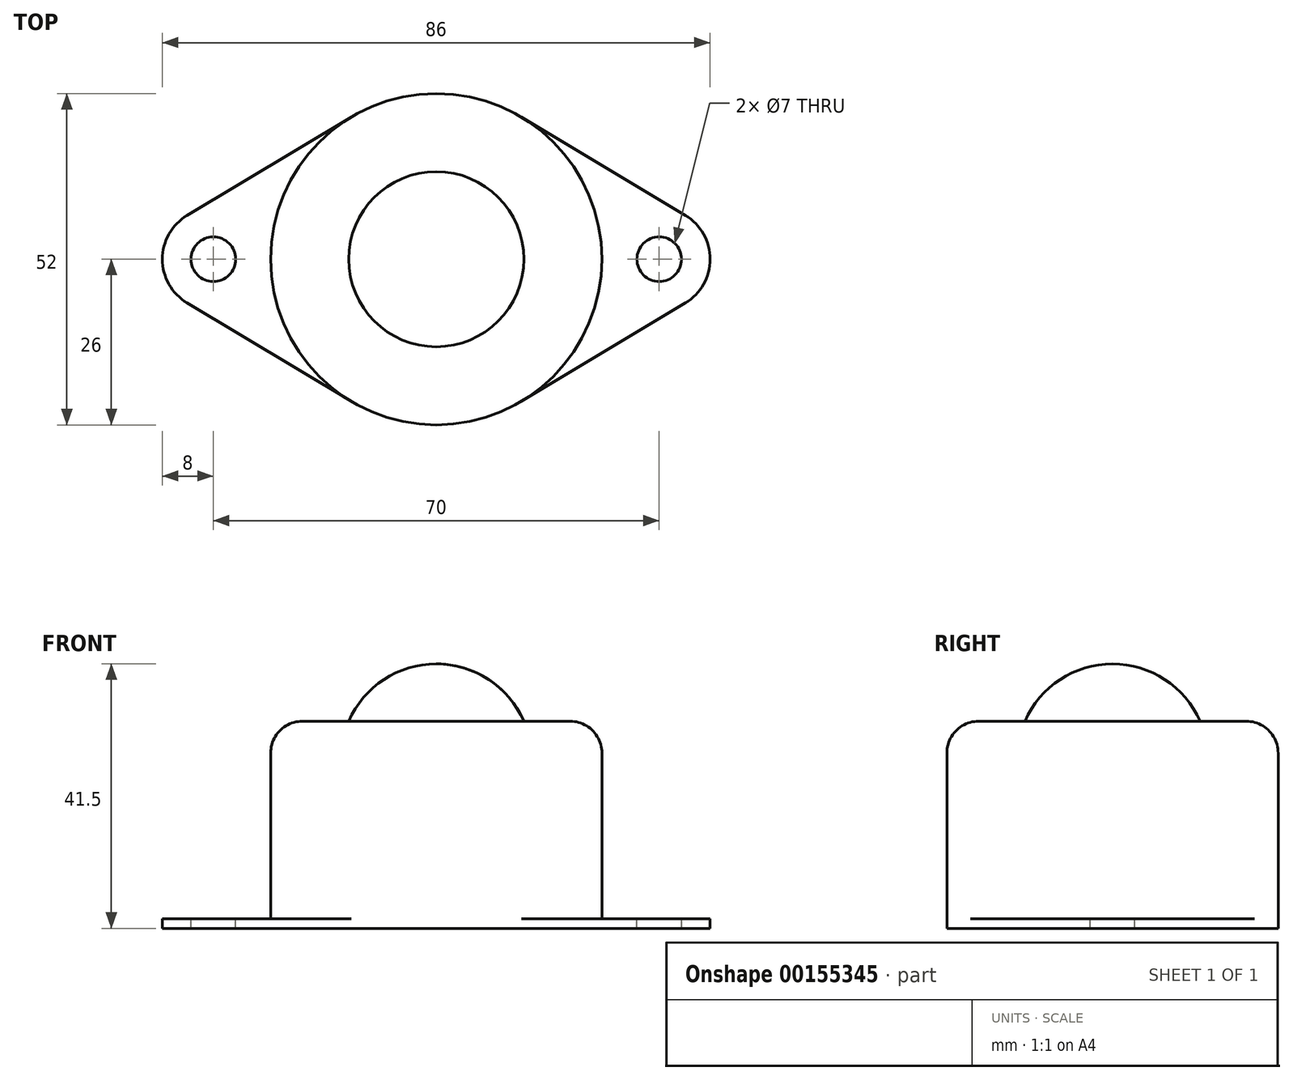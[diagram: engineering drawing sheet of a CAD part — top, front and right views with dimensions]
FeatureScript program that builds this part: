
annotation { "Feature Type Name" : "Feature", "Feature Type Description" : "" }
export const myFeature = defineFeature(function(context is Context, id is Id, definition is map)
    precondition{}
    {
        {
            var Q0;
            Q0=qCreatedBy(makeId("Front.planeOp"),FACE);
            var sketch = newSketch(context, id + "F0", { "sketchPlane" : qUnion([Q0])});
            skArc(sketch, "E0", {"start": v(0, 15) * mm, "mid": v(-8.22, 12.55) * mm, "end": v(-13.75, 6) * mm});
            skLineSegment(sketch, "E1.bottom", {"start": v(-21, 6) * mm, "end": v(-13.75, 6) * mm});
            skLineSegment(sketch, "E1.top", {"start": v(-26, -25) * mm, "end": v(0, -25) * mm});
            skLineSegment(sketch, "E1.left", {"start": v(-26, 1) * mm, "end": v(-26, -23.5) * mm});
            skPoint(sketch, "E2.visualSharp", {"position": v(-26, 6) * mm});
            skArc(sketch, "E2.filletArc", {"start": v(-21, 6) * mm, "mid": v(-24.54, 4.54) * mm, "end": v(-26, 1) * mm});
            skPoint(sketch, "E3.orphan", {"position": v(0, 6) * mm});
            skLineSegment(sketch, "E4", {"start": v(0, -25) * mm, "end": v(0, 15) * mm});
            skLineSegment(sketch, "E5", {"start": v(-26, -23.5) * mm, "end": v(-26, -25) * mm});
            skSolve(sketch);
        }
        {
            var Q0;
            Q0=makeQuery(id+"F0.imprint","IMPRINT",FACE,{"disambiguationData":[TD([[makeQuery(id+"F0.imprint","IMPRINT",EDGE,{"derivedFrom":sQuery(id+"F0.wireOp",EDGE,"E0")}),1.0]])]});
            var Q1;
            Q1=sQuery(id+"F0.wireOp",EDGE,"E4");
            revolve(context, id + "F1", {"entities" : qUnion([Q0]), "axis" : qUnion([Q1]), "revolveType" : RevolveType.FULL});
        }
        {
            var Q0;
            Q0=makeQuery(id+"F1.opRevolve","SWEPT_FACE",FACE,{"disambiguationData":[OSD([sQuery(id+"F0.wireOp",EDGE,"E1.top")])]});
            var sketch = newSketch(context, id + "F2", { "sketchPlane" : qUnion([Q0])});
            skArc(sketch, "E6", {"start": v(-13.37, -22.3) * mm, "mid": v(0, -26) * mm, "end": v(13.37, -22.3) * mm});
            skLineSegment(sketch, "E7", {"start": v(0, 31.62) * mm, "end": v(0, -33.16) * mm, "construction": true});
            skLineSegment(sketch, "E8", {"start": v(0, 0) * mm, "end": v(-35, 0) * mm, "construction": true});
            skCircle(sketch, "E9", {"center": v(-35, 0) * mm, "radius": 3.5 * mm});
            skArc(sketch, "E10", {"start": v(-39.11, 6.86) * mm, "mid": v(-43, 0) * mm, "end": v(-39.11, -6.86) * mm});
            skLineSegment(sketch, "E11", {"start": v(-13.37, 22.3) * mm, "end": v(-39.11, 6.86) * mm});
            skLineSegment(sketch, "E12.MirrorCS", {"start": v(-13.37, -22.3) * mm, "end": v(-39.11, -6.86) * mm});
            skLineSegment(sketch, "E13.MirrorCS", {"start": v(13.37, 22.3) * mm, "end": v(39.11, 6.86) * mm});
            skArc(sketch, "E14.MirrorC", {"start": v(39.11, 6.86) * mm, "mid": v(43, 0) * mm, "end": v(39.11, -6.86) * mm});
            skLineSegment(sketch, "E15.MirrorCS", {"start": v(13.37, -22.3) * mm, "end": v(39.11, -6.86) * mm});
            skArc(sketch, "E16.trimOffspring", {"start": v(13.37, 22.3) * mm, "mid": v(0, 26) * mm, "end": v(-13.37, 22.3) * mm});
            skCircle(sketch, "E17.MirrorC", {"center": v(35, 0) * mm, "radius": 3.5 * mm});
            skSolve(sketch);
        }
        {
            var Q0;
            Q0 = qSketchRegion(id + "F2", true);
            extrude(context, id + "F3", {"entities" : qUnion([Q0]), "operationType" : NewBodyOperationType.ADD, "depth" : 1.5 * mm});
        }
    });
